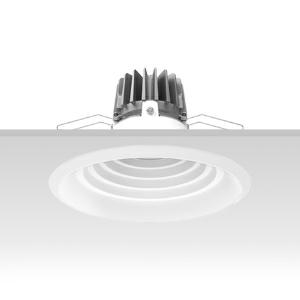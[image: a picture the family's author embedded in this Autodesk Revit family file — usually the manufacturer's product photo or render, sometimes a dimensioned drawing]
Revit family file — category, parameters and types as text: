
# Revit family: 3f_filippi_-_3f_reno_bianco_ampio_3f_filippi_-_30625_-_3f_reno_200_wh_2000-930_wide
name_source: partatom
category: Lighting Fixtures
units: mm (PartAtom-declared; Revit-internal decimal feet)

## family parameters
Cut with Voids When Loaded = No
Host = Face
Light Source = No
Part Type = Normal
Room Calculation Point = No
Round Connector Dimension = Use Diameter
Shared = No

## types (1)
- 3F Filippi - 3F Reno Bianco Ampio (1 x LED, 1880 lm, 24 W, 3000 K)
    Apparent Load = 24 VA
    Approval mark = CE
    CIE Flux Codes = 80 97 100 100 100
    Color Rendering = 90
    Color Temperature = 3000 K
    Control Gear = Electronic ballast
    Default Elevation = 1800 mm
    Description = ILLUMINOTECHNICAL
Luminous efficiency 100% (DLOR 100%, ULOR 0%).
Initial luminous flux of the luminaire 1880 lm.
Direct symmetric wide distribution.
Installation Interdistance Transv.D = 1.56 x hu - Long.D = 1.56 x hu.
Average luminance <3000 cd/m² for radial angles >65°.
Tabular UGR (CIE 117 - 4H-8H; S=0.25H; 70/50/20): RUG 19.2 - 19.2.
Beam angle: 85° - 84°.
Luminous efficacy 78 lm/W.
Lifetime (L90/B10): 30000 h. (tq+25°C)
Lifetime (L85/B10): 50000 h. (tq+25°C)
Lifetime (L70/B10): 80000 h. (tq+25°C)
Sudden decreased luminous flux after 50000 hours: 0% (C0).
Photobiological safety in compliance with IEC/TR 62778: RG0 risk exempt, (IEC 62471).
In compliance with IEC/EN 62722-2-1 - IEC/EN 62717 standards.

SOURCE
Compact LED module 2000/930.
Energy efficiency class (UE 2019/2020 - UE 2019/2015): E.
CIE 13.3 Colour rendering index: CRI >90 (R9 >50%).
IES TM-30 Fidelity Index: Rf = 92 Rg = 101.
CCT nominal colour temperature 3000 K.
Colour initial tolerance (MacAdam): SDCM 3.
Zhaga Book 3 compliant.

MECHANICAL
Passive heat dissipator in die-casting aluminium, oversized, for optimum thermal management of the LED module.
Parabolic element with graduated/concentric rings in white polycarbonate.
Transparent external lens with glossy and satin differentiated surfaces, with a cooling and anti-insect system in methacrylate (PMMA).
Fastening spring clips in stainless steel.
Dimensions: diameter 216 mm, height 142 mm. Weight 0.81 kg.
IP44 protection degree for exposed part, IP20 for recessed part.
Mechanical strength to impacts IK04 (0.5 joule).
Glow-wire test resistance 650°C.

ELECTRICAL
Wiring on a separate unit.
Halogen Free electronic wiring 230V-50/60Hz, power factor 0.95, THD <25%, constant output current, SELV, class II, 1 driver.
Power of the luminaire 24 W.
ENEC - CE.
SAFE FLICKER: PstLM=<1 and SVM=<0.4 (IEC TR 61547-1 and IEC TR 63158), to ensure a more comfortable and safe light.
Luminaire compliant with EN 60598-2-22 for power supply from a centralised emergency system CPSS (Central Power Supply System), not incorporated in the luminaire - high risk areas excluded. The default power and flux are 100% in AC and 100% in DC.
Ambient temperature from 0°C to +25°C.
Temperature class T6 max 85°C.
Relative humidity UR: <85%.

INSTALLATION
Pull-up recessed fitting.
False ceiling carving: 200 mm.
All accessories dedicated to this product are available on the Catalog and on our website www.3F-Filippi.com.

APPLICATIONS
Environments: architectural, commercial, exhibition areas, transit areas, corridors, shops, display windows, service areas.
In false ceilings with narrow voids.

WARNING
Luminaire designed for disposal/recycling at end-of-life.
Replaceable (LED only) light source by a professional. Replaceable control gear by a professional.
    Height = 0 mm  [stored 0 ft]
    Lamp = 1 x LED
    Lamp Light Flux = 1880 lm
    Lamp Power = 24 W
    Lamp count = 1
    Length = 216 mm
    Lifetime = 50000 h
    Luminous efficacy = 78 lm/W
    Manufacturer = 3F Filippi
    ModVariant = No
    Model = 3F Filippi - 30625 - 3F Reno 200 WH 2000-930 WIDE
    Mounting Place = Ceiling
    Mounting Type = Recessed
    Number of Poles = 1
    OnlyDefault = Yes
    Power Factor = 1
    Product Name = 3F Filippi - 3F Reno Bianco Ampio
    Product group = recessed luminaire
    ProductGroupID = 4
    Protection Class = Protection class II
    Protection Degree = IP 20
    RLX_Detail_Level = 1
    RLX_Emergency_Light_Flux = 0 lm
    RLX_Emergency_Type = 0
    RLX_Emergency_Type_DB = No
    RlxData = <blob elided: 87693 chars, md5=9caefeac>
    Socket = socket
    Standby Power = 0 W
    System Light Flux = 1880 lm
    System Power = 24 W
    Type Comments = Product without accessories
    Type Image = 3ffilippi_3f_reno_200_wh_2000.jpg
    URL = http://relux.com
    VarID = ---
    Voltage = 0 V
    Weight = 0.00 kg
    Width = 0 mm  [stored 0 ft]

note: [stored X ft] marks values corroborated as IEEE doubles in the binary element streams (Revit-internal decimal feet)

## geometry (parser evidence)
native form markers: Blend x4, Sweep x9
no freeform markers — native parametric forms only
